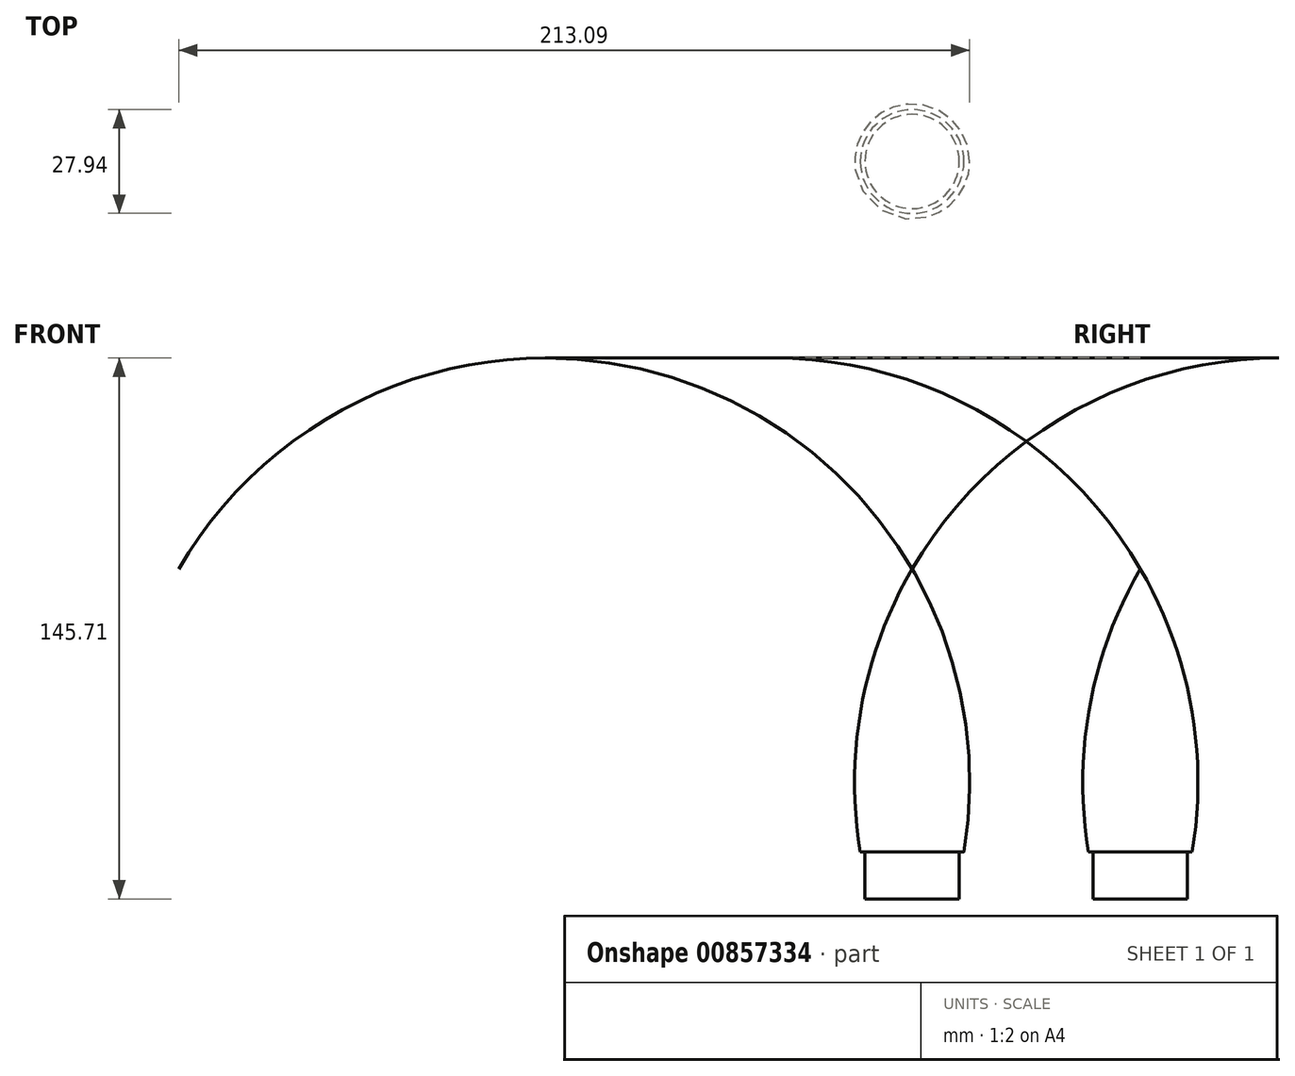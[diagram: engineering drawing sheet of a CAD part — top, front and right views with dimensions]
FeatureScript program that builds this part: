
annotation { "Feature Type Name" : "Feature", "Feature Type Description" : "" }
export const myFeature = defineFeature(function(context is Context, id is Id, definition is map)
    precondition{}
    {
        {
            var Q0;
            Q0=qCreatedBy(makeId("Front.planeOp"),FACE);
            var sketch = newSketch(context, id + "F0", { "sketchPlane" : qUnion([Q0])});
            skLineSegment(sketch, "E0", {"start": v(0, 0) * mm, "end": v(0, 76.2) * mm});
            skLineSegment(sketch, "E1", {"start": v(0, 0) * mm, "end": v(13.97, 0) * mm});
            skArc(sketch, "E2", {"start": v(13.97, 0) * mm, "mid": v(13.64, 39.32) * mm, "end": v(0, 76.2) * mm});
            skSolve(sketch);
        }
        {
            var Q0;
            Q0 = qSketchRegion(id + "F0", true);
            var Q1;
            Q1=sQuery(id+"F0.wireOp",EDGE,"E0");
            revolve(context, id + "F1", {"surfaceOperationType" : NewSurfaceOperationType.NEW, "entities" : qUnion([Q0]), "axis" : qUnion([Q1]), "revolveType" : RevolveType.FULL});
        }
        {
            var Q0;
            Q0=makeQuery(id+"F1.opRevolve","SWEPT_FACE",FACE,{"disambiguationData":[OSD([sQuery(id+"F0.wireOp",EDGE,"E1")])]});
            var sketch = newSketch(context, id + "F2", { "sketchPlane" : qUnion([Q0])});
            skCircle(sketch, "E3", {"center": v(0, 0) * mm, "radius": 12.7 * mm});
            skSolve(sketch);
        }
        {
            var Q0;
            Q0=makeQuery(id+"F2.imprint","IMPRINT",FACE,{"disambiguationData":[TD([[makeQuery(id+"F2.imprint","IMPRINT",EDGE,{"derivedFrom":sQuery(id+"F2.wireOp",EDGE,"E3")}),1.0]])]});
            extrude(context, id + "F3", {"entities" : qUnion([Q0]), "operationType" : NewBodyOperationType.ADD, "depth" : 12.7 * mm, "offsetDistance" : 25.4 * mm});
        }
    });
